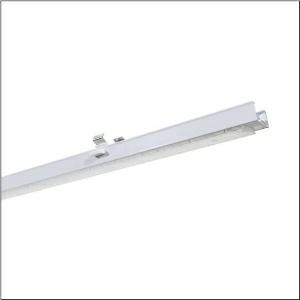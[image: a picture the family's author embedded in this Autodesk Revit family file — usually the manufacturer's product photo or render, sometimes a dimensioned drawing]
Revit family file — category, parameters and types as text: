
# Revit family: sanierungs-leuchteneinsatz_31_gen_2_51re14mb68b_e618
name_source: partatom
category: Lighting Fixtures
units: mm (PartAtom-declared; Revit-internal decimal feet)

## family parameters
Cut with Voids When Loaded = No
Host = Face
Light Source = No
Part Type = Normal
Room Calculation Point = No
Round Connector Dimension = Use Diameter
Shared = No

## types (1)
- --- (1 x LED, 8000 lm, 50 W, 6500K)
    Apparent Load = 50 VA
    CIE Flux Codes = 72 92 98 99 100
    Color Rendering = 80
    Color Temperature = 6500K
    Default Elevation = 1800 mm
    Description = Refurbishment luminaire insert Gen.2, luminaire insert, of extruded aluminium section, coated, traffic white (RAL 9016), length: 1.472mm, width: 91mm, height: 53mm, LED rated luminous flux: 8.000lm, light colour: 865, control gear: ON/OFF Multilumen, control gear: ECG Multilumen, with system connector: socket, mains connection: 220..240V, AC/DC, 0/50..60Hz, luminous flux adjustable on luminaire in four steps (4280/5650/6950/8270lm), connected load according to luminous flux setting (24/32/40/49W), primary light control with lens, of plastic, primary optical cover: cover, of PMMA, light emission: direct distribution, primary light characteristic: asymmetric, protection rating (complete): IP20, insulation class (complete): insulation class I (protective earthing), certification: CE, UKCA, permissible ambient temperature for indoor applications: -20..+40°C, packaging unit: 1 piece
    Height = 58 mm
    Lamp = 1 x LED
    Lamp Light Flux = 8000 lm
    Lamp Power = 50 W
    Lamp count = 1
    Length = 1472 mm
    Luminous efficacy = 160 lm/W
    Manufacturer = Siteco
    ModVariant = No
    Model = 51RE14MB68B
    Mounting Place = Ceiling
    Mounting Type = Pendant
    Number of Poles = 1
    OnlyDefault = Yes
    Power Factor = 1
    Product Name = Sanierungs-Leuchteneinsatz 31 Gen.2
    Product group = luminaire insert
    ProductGroupID = 902
    Protection Class = Protection class I
    Protection Degree = IP 20
    RLX_Detail_Level = 1
    RlxData = <blob elided: 21061 chars, md5=48310268>
    Socket = socket
    Standby Power = 0 W
    System Light Flux = 8000 lm
    System Power = 50 W
    Type Comments = factory setting: luminous flux: 100 % | (ON | ON) | 300 mA
    Type Image = l_1266702.jpg
    URL = http://relux.com
    VarID = @adj_090949
    Voltage = 0 V
    Weight = 0.00 kg
    Width = 65 mm

## geometry (parser evidence)
native form markers: Blend x4, Sweep x10
no freeform markers — native parametric forms only
